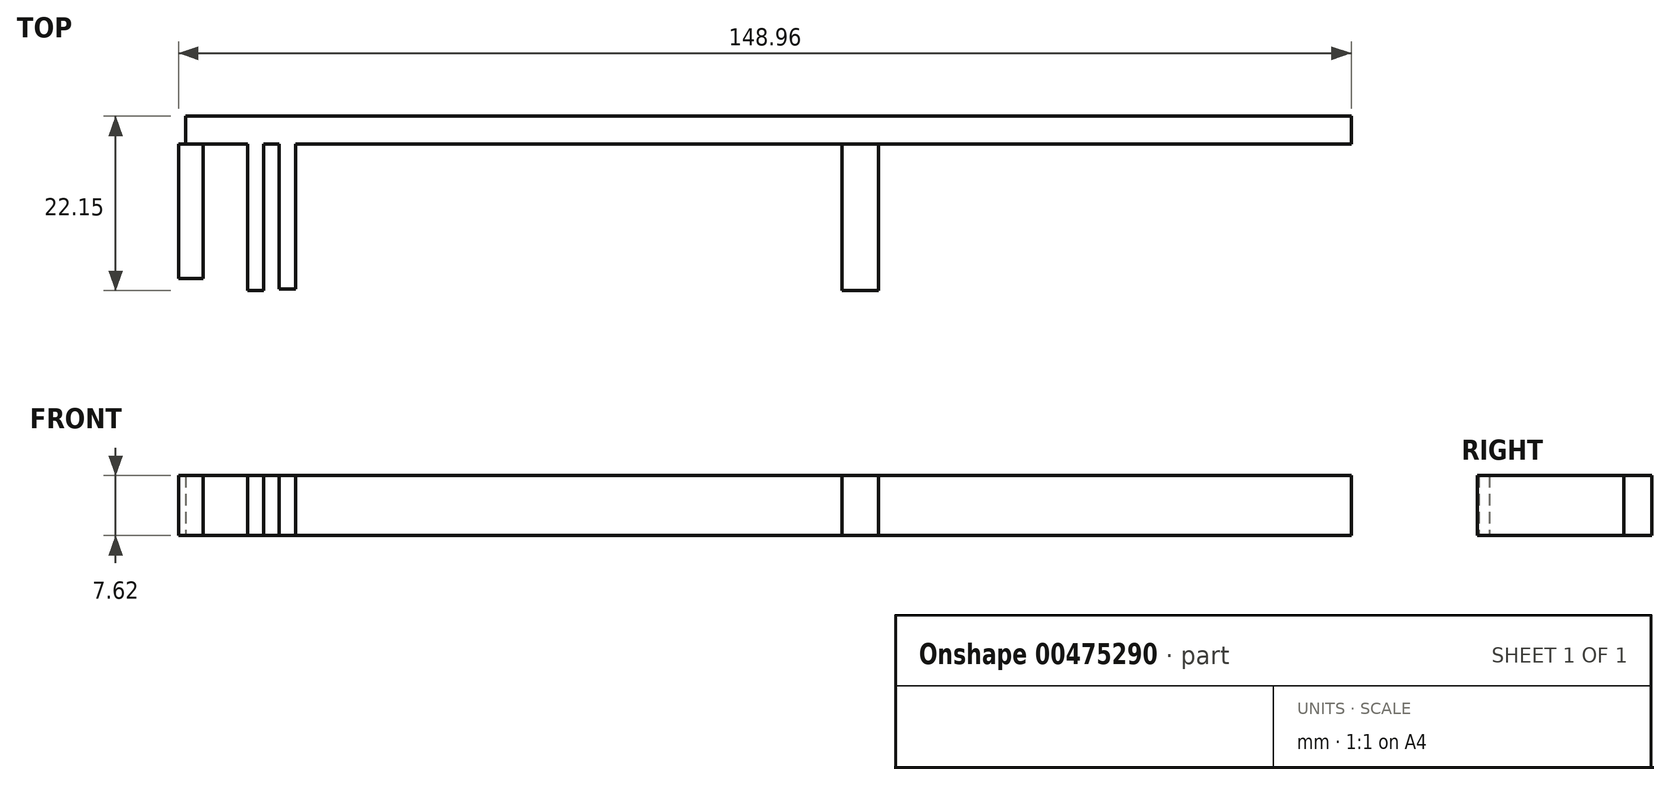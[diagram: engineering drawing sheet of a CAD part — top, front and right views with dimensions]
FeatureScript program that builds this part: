
annotation { "Feature Type Name" : "Feature", "Feature Type Description" : "" }
export const myFeature = defineFeature(function(context is Context, id is Id, definition is map)
    precondition{}
    {
        {
            var Q0;
            Q0=qCreatedBy(makeId("Top.planeOp"),FACE);
            var sketch = newSketch(context, id + "F0", { "sketchPlane" : qUnion([Q0])});
            skLineSegment(sketch, "E0.bottom", {"start": v(-73.45, 48.53) * mm, "end": v(74.62, 48.53) * mm});
            skLineSegment(sketch, "E0.top", {"start": v(-73.45, 45.03) * mm, "end": v(74.62, 45.03) * mm});
            skLineSegment(sketch, "E0.left", {"start": v(-73.45, 48.53) * mm, "end": v(-73.45, 45.03) * mm});
            skLineSegment(sketch, "E0.right", {"start": v(74.62, 48.53) * mm, "end": v(74.62, 45.03) * mm});
            skSolve(sketch);
        }
        {
            var Q0;
            Q0=makeQuery(id+"F0.imprint","IMPRINT",FACE,{"disambiguationData":[TD([[makeQuery(id+"F0.imprint","IMPRINT",EDGE,{"derivedFrom":sQuery(id+"F0.wireOp",EDGE,"E0.bottom")}),-1.0]])]});
            extrude(context, id + "F1", {"entities" : qUnion([Q0]), "depth" : 7.62 * mm});
        }
        {
            var Q0;
            Q0=qCreatedBy(makeId("Top.planeOp"),FACE);
            var sketch = newSketch(context, id + "F2", { "sketchPlane" : qUnion([Q0])});
            skLineSegment(sketch, "E1.bottom", {"start": v(-74.34, 45.03) * mm, "end": v(-71.22, 45.03) * mm});
            skLineSegment(sketch, "E1.top", {"start": v(-74.34, 27.93) * mm, "end": v(-71.22, 27.93) * mm});
            skLineSegment(sketch, "E1.left", {"start": v(-74.34, 45.03) * mm, "end": v(-74.34, 27.93) * mm});
            skLineSegment(sketch, "E1.right", {"start": v(-71.22, 45.03) * mm, "end": v(-71.22, 27.93) * mm});
            skSolve(sketch);
        }
        {
            var Q0;
            Q0=makeQuery(id+"F2.imprint","IMPRINT",FACE,{"disambiguationData":[TD([[makeQuery(id+"F2.imprint","IMPRINT",EDGE,{"derivedFrom":sQuery(id+"F2.wireOp",EDGE,"E1.bottom")}),-1.0]])]});
            extrude(context, id + "F3", {"entities" : qUnion([Q0]), "depth" : 7.62 * mm});
        }
        {
            var Q0;
            Q0=qCreatedBy(makeId("Top.planeOp"),FACE);
            var sketch = newSketch(context, id + "F4", { "sketchPlane" : qUnion([Q0])});
            skLineSegment(sketch, "E2.bottom", {"start": v(14.57, 45.03) * mm, "end": v(9.91, 45.03) * mm});
            skLineSegment(sketch, "E2.top", {"start": v(14.57, 26.38) * mm, "end": v(9.91, 26.38) * mm});
            skLineSegment(sketch, "E2.left", {"start": v(14.57, 45.03) * mm, "end": v(14.57, 26.38) * mm});
            skLineSegment(sketch, "E2.right", {"start": v(9.91, 45.03) * mm, "end": v(9.91, 26.38) * mm});
            skSolve(sketch);
        }
        {
            var Q0;
            Q0=makeQuery(id+"F4.imprint","IMPRINT",FACE,{"disambiguationData":[TD([[makeQuery(id+"F4.imprint","IMPRINT",EDGE,{"derivedFrom":sQuery(id+"F4.wireOp",EDGE,"E2.bottom")}),1.0]])]});
            extrude(context, id + "F5", {"entities" : qUnion([Q0]), "depth" : 7.62 * mm});
        }
        {
            var Q0;
            Q0=qCreatedBy(makeId("Top.planeOp"),FACE);
            var sketch = newSketch(context, id + "F6", { "sketchPlane" : qUnion([Q0])});
            skLineSegment(sketch, "E3.bottom", {"start": v(-65.58, 45.03) * mm, "end": v(-63.54, 45.03) * mm});
            skLineSegment(sketch, "E3.top", {"start": v(-65.58, 26.38) * mm, "end": v(-63.54, 26.38) * mm});
            skLineSegment(sketch, "E3.left", {"start": v(-65.58, 45.03) * mm, "end": v(-65.58, 26.38) * mm});
            skLineSegment(sketch, "E3.right", {"start": v(-63.54, 45.03) * mm, "end": v(-63.54, 26.38) * mm});
            skSolve(sketch);
        }
        {
            var Q0;
            Q0=makeQuery(id+"F6.imprint","IMPRINT",FACE,{"disambiguationData":[TD([[makeQuery(id+"F6.imprint","IMPRINT",EDGE,{"derivedFrom":sQuery(id+"F6.wireOp",EDGE,"E3.bottom")}),-1.0]])]});
            extrude(context, id + "F7", {"entities" : qUnion([Q0]), "operationType" : NewBodyOperationType.ADD, "depth" : 7.62 * mm});
        }
        {
            var Q0;
            Q0=qCreatedBy(makeId("Top.planeOp"),FACE);
            var sketch = newSketch(context, id + "F8", { "sketchPlane" : qUnion([Q0])});
            skLineSegment(sketch, "E4.bottom", {"start": v(-61.57, 45.03) * mm, "end": v(-59.5, 45.03) * mm});
            skLineSegment(sketch, "E4.top", {"start": v(-61.57, 26.57) * mm, "end": v(-59.5, 26.57) * mm});
            skLineSegment(sketch, "E4.left", {"start": v(-59.5, 45.03) * mm, "end": v(-59.5, 26.57) * mm});
            skLineSegment(sketch, "E4.right", {"start": v(-61.57, 45.03) * mm, "end": v(-61.57, 26.57) * mm});
            skSolve(sketch);
        }
        {
            var Q0;
            Q0=makeQuery(id+"F8.imprint","IMPRINT",FACE,{"disambiguationData":[TD([[makeQuery(id+"F8.imprint","IMPRINT",EDGE,{"derivedFrom":sQuery(id+"F8.wireOp",EDGE,"E4.bottom")}),-1.0]])]});
            extrude(context, id + "F9", {"entities" : qUnion([Q0]), "operationType" : NewBodyOperationType.ADD, "depth" : 7.62 * mm});
        }
    });
